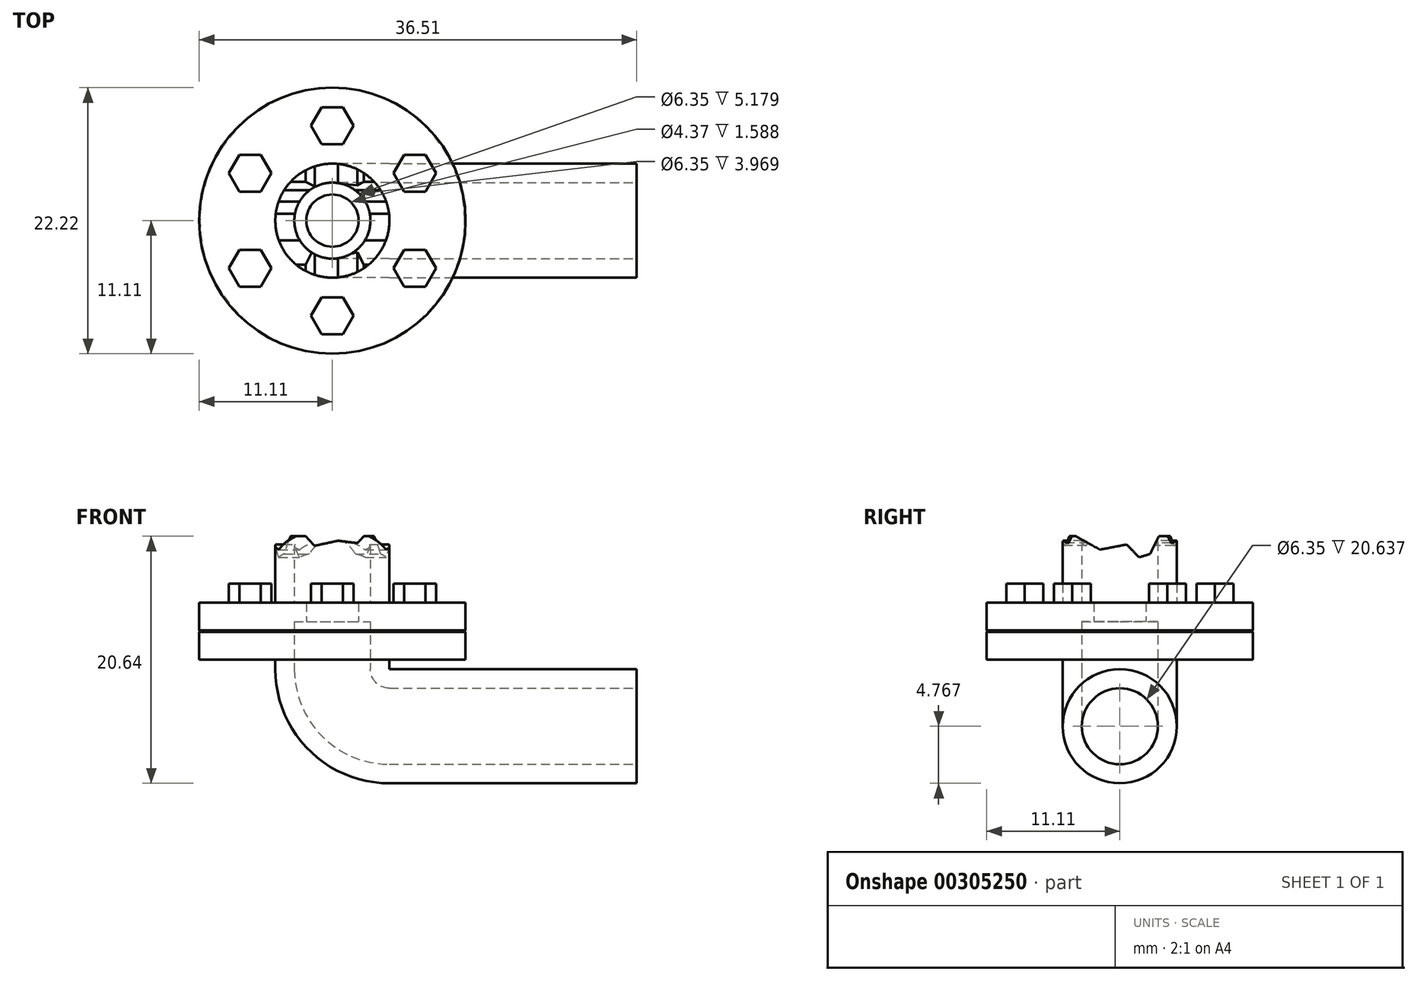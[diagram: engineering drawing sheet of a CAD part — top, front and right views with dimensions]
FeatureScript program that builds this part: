
annotation { "Feature Type Name" : "Feature", "Feature Type Description" : "" }
export const myFeature = defineFeature(function(context is Context, id is Id, definition is map)
    precondition{}
    {
        {
            var Q0;
            Q0=qCreatedBy(makeId("Front.planeOp"),FACE);
            var sketch = newSketch(context, id + "F0", { "sketchPlane" : qUnion([Q0])});
            skLineSegment(sketch, "E0", {"start": v(0, 0) * mm, "end": v(0, 11.11) * mm, "construction": true});
            skLineSegment(sketch, "E1", {"start": v(3.17, 11.11) * mm, "end": v(4.76, 11.11) * mm});
            skLineSegment(sketch, "E2", {"start": v(4.76, 11.11) * mm, "end": v(4.76, 5.56) * mm});
            skLineSegment(sketch, "E3", {"start": v(4.76, 5.56) * mm, "end": v(11.11, 5.56) * mm});
            skLineSegment(sketch, "E4", {"start": v(11.11, 5.56) * mm, "end": v(11.11, 3.24) * mm});
            skLineSegment(sketch, "E5", {"start": v(11.11, 3.24) * mm, "end": v(11.05, 3.18) * mm});
            skLineSegment(sketch, "E6", {"start": v(11.05, 3.18) * mm, "end": v(11.11, 3.11) * mm});
            skLineSegment(sketch, "E7", {"start": v(11.11, 3.11) * mm, "end": v(11.11, 0.8) * mm});
            skLineSegment(sketch, "E8", {"start": v(11.11, 0.8) * mm, "end": v(4.76, 0.8) * mm});
            skLineSegment(sketch, "E9", {"start": v(4.76, 0.8) * mm, "end": v(4.76, 0) * mm});
            skLineSegment(sketch, "E10", {"start": v(4.76, 0) * mm, "end": v(3.18, 0) * mm});
            skLineSegment(sketch, "E11", {"start": v(3.18, 0) * mm, "end": v(3.17, 5.56) * mm});
            skLineSegment(sketch, "E12", {"start": v(3.17, 5.56) * mm, "end": v(2.18, 5.56) * mm});
            skLineSegment(sketch, "E13", {"start": v(2.18, 3.97) * mm, "end": v(2.18, 5.56) * mm});
            skLineSegment(sketch, "E14", {"start": v(2.18, 3.97) * mm, "end": v(3.17, 3.97) * mm});
            skLineSegment(sketch, "E15", {"start": v(3.18, 3.97) * mm, "end": v(3.17, 11.11) * mm});
            skPoint(sketch, "E16", {"position": v(2.18, 4.76) * mm});
            skSolve(sketch);
        }
        {
            var Q0;
            {var subQ0=sQuery(id+"F0.wireOp",EDGE,"E1");Q0=makeQuery(id+"F0.imprint","IMPRINT",FACE,{"disambiguationData":[TD([[makeQuery(id+"F0.imprint","IMPRINT",EDGE,{"derivedFrom":subQ0}),-1.0]])]});}
            var Q1;
            {var subQ0=sQuery(id+"F0.wireOp",EDGE,"E12");Q1=makeQuery(id+"F0.imprint","IMPRINT",FACE,{"disambiguationData":[TD([[makeQuery(id+"F0.imprint","IMPRINT",EDGE,{"derivedFrom":subQ0}),1.0]])]});}
            var Q2;
            Q2=sQuery(id+"F0.wireOp",EDGE,"E0");
            revolve(context, id + "F1", {"entities" : qUnion([Q0, Q1]), "axis" : qUnion([Q2]), "revolveType" : RevolveType.FULL});
        }
        {
            var Q0;
            Q0=makeQuery(id+"F1.opRevolve","SWEPT_FACE",FACE,{"disambiguationData":[OSD([sQuery(id+"F0.wireOp",EDGE,"E3")])]});
            var sketch = newSketch(context, id + "F2", { "sketchPlane" : qUnion([Q0])});
            skCircle(sketch, "E17.cCircle", {"center": v(0, 7.94) * mm, "radius": 1.54 * mm, "construction": true});
            skLineSegment(sketch, "E17.0", {"start": v(-0.89, 9.48) * mm, "end": v(0.89, 9.48) * mm});
            skLineSegment(sketch, "E17.1", {"start": v(0.89, 9.48) * mm, "end": v(1.78, 7.94) * mm});
            skLineSegment(sketch, "E17.2", {"start": v(1.78, 7.94) * mm, "end": v(0.89, 6.4) * mm});
            skLineSegment(sketch, "E17.3", {"start": v(0.89, 6.4) * mm, "end": v(-0.89, 6.4) * mm});
            skLineSegment(sketch, "E17.4", {"start": v(-0.89, 6.4) * mm, "end": v(-1.78, 7.94) * mm});
            skLineSegment(sketch, "E17.5", {"start": v(-1.78, 7.94) * mm, "end": v(-0.89, 9.48) * mm});
            skPoint(sketch, "E17.0.midPoint", {"position": v(0, 9.48) * mm});
            skLineSegment(sketch, "E18", {"start": v(0, 4.76) * mm, "end": v(0, 11.11) * mm, "construction": true});
            skLineSegment(sketch, "E19.1.0", {"start": v(-8.65, 3.97) * mm, "end": v(-7.76, 5.5) * mm});
            skLineSegment(sketch, "E19.1.1", {"start": v(-7.76, 2.43) * mm, "end": v(-8.65, 3.97) * mm});
            skLineSegment(sketch, "E19.1.2", {"start": v(-5.99, 2.43) * mm, "end": v(-7.76, 2.43) * mm});
            skLineSegment(sketch, "E19.1.3", {"start": v(-5.1, 3.97) * mm, "end": v(-5.99, 2.43) * mm});
            skLineSegment(sketch, "E19.1.4", {"start": v(-5.99, 5.5) * mm, "end": v(-5.1, 3.97) * mm});
            skLineSegment(sketch, "E19.1.5", {"start": v(-7.76, 5.5) * mm, "end": v(-5.99, 5.5) * mm});
            skLineSegment(sketch, "E19.2.0", {"start": v(-7.76, -5.5) * mm, "end": v(-8.65, -3.97) * mm});
            skLineSegment(sketch, "E19.2.1", {"start": v(-5.99, -5.5) * mm, "end": v(-7.76, -5.5) * mm});
            skLineSegment(sketch, "E19.2.2", {"start": v(-5.1, -3.97) * mm, "end": v(-5.99, -5.5) * mm});
            skLineSegment(sketch, "E19.2.3", {"start": v(-5.99, -2.43) * mm, "end": v(-5.1, -3.97) * mm});
            skLineSegment(sketch, "E19.2.4", {"start": v(-7.76, -2.43) * mm, "end": v(-5.99, -2.43) * mm});
            skLineSegment(sketch, "E19.2.5", {"start": v(-8.65, -3.97) * mm, "end": v(-7.76, -2.43) * mm});
            skLineSegment(sketch, "E19.3.0", {"start": v(0.89, -9.48) * mm, "end": v(-0.89, -9.48) * mm});
            skLineSegment(sketch, "E19.3.1", {"start": v(1.78, -7.94) * mm, "end": v(0.89, -9.48) * mm});
            skLineSegment(sketch, "E19.3.2", {"start": v(0.89, -6.4) * mm, "end": v(1.78, -7.94) * mm});
            skLineSegment(sketch, "E19.3.3", {"start": v(-0.89, -6.4) * mm, "end": v(0.89, -6.4) * mm});
            skLineSegment(sketch, "E19.3.4", {"start": v(-1.78, -7.94) * mm, "end": v(-0.89, -6.4) * mm});
            skLineSegment(sketch, "E19.3.5", {"start": v(-0.89, -9.48) * mm, "end": v(-1.78, -7.94) * mm});
            skLineSegment(sketch, "E19.4.0", {"start": v(8.65, -3.97) * mm, "end": v(7.76, -5.5) * mm});
            skLineSegment(sketch, "E19.4.1", {"start": v(7.76, -2.43) * mm, "end": v(8.65, -3.97) * mm});
            skLineSegment(sketch, "E19.4.2", {"start": v(5.99, -2.43) * mm, "end": v(7.76, -2.43) * mm});
            skLineSegment(sketch, "E19.4.3", {"start": v(5.1, -3.97) * mm, "end": v(5.99, -2.43) * mm});
            skLineSegment(sketch, "E19.4.4", {"start": v(5.99, -5.5) * mm, "end": v(5.1, -3.97) * mm});
            skLineSegment(sketch, "E19.4.5", {"start": v(7.76, -5.5) * mm, "end": v(5.99, -5.5) * mm});
            skLineSegment(sketch, "E19.5.0", {"start": v(7.76, 5.5) * mm, "end": v(8.65, 3.97) * mm});
            skLineSegment(sketch, "E19.5.1", {"start": v(5.99, 5.5) * mm, "end": v(7.76, 5.5) * mm});
            skLineSegment(sketch, "E19.5.2", {"start": v(5.1, 3.97) * mm, "end": v(5.99, 5.5) * mm});
            skLineSegment(sketch, "E19.5.3", {"start": v(5.99, 2.43) * mm, "end": v(5.1, 3.97) * mm});
            skLineSegment(sketch, "E19.5.4", {"start": v(7.76, 2.43) * mm, "end": v(5.99, 2.43) * mm});
            skLineSegment(sketch, "E19.5.5", {"start": v(8.65, 3.97) * mm, "end": v(7.76, 2.43) * mm});
            skPoint(sketch, "E19.center", {"position": v(0, 0) * mm});
            skSolve(sketch);
        }
        {
            var Q0;
            Q0 = qSketchRegion(id + "F2", true);
            extrude(context, id + "F3", {"entities" : qUnion([Q0]), "operationType" : NewBodyOperationType.ADD, "depth" : 1.59 * mm});
        }
        {
            var Q0;
            Q0=qCreatedBy(makeId("Right.planeOp"),FACE);
            var sketch = newSketch(context, id + "F4", { "sketchPlane" : qUnion([Q0])});
            skLineSegment(sketch, "E20", {"start": v(-4.76, 5.56) * mm, "end": v(-4.76, 11.11) * mm});
            skLineSegment(sketch, "E21", {"start": v(4.76, 11.11) * mm, "end": v(4.76, 5.56) * mm});
            skLineSegment(sketch, "E22", {"start": v(3.25, 11.11) * mm, "end": v(2.53, 9.63) * mm});
            skLineSegment(sketch, "E23", {"start": v(2.53, 9.63) * mm, "end": v(1.6, 9.35) * mm});
            skLineSegment(sketch, "E24", {"start": v(1.6, 9.35) * mm, "end": v(0.58, 10.42) * mm});
            skLineSegment(sketch, "E25", {"start": v(0.58, 10.42) * mm, "end": v(-1.65, 9.99) * mm});
            skLineSegment(sketch, "E26", {"start": v(-1.65, 9.99) * mm, "end": v(-3.69, 11.11) * mm});
            skLineSegment(sketch, "E27", {"start": v(-3.69, 11.11) * mm, "end": v(3.25, 11.11) * mm});
            skLineSegment(sketch, "E28.0.0", {"start": v(-4.76, 11.11) * mm, "end": v(4.76, 11.11) * mm});
            skSolve(sketch);
        }
        {
            var Q0;
            Q0 = qSketchRegion(id + "F4", true);
            extrude(context, id + "F5", {"entities" : qUnion([Q0]), "operationType" : NewBodyOperationType.REMOVE, "oppositeDirection" : true, "depth" : 25.4 * mm, "symmetric" : true});
        }
        {
            var Q0;
            Q0=qCreatedBy(makeId("Front.planeOp"),FACE);
            var sketch = newSketch(context, id + "F6", { "sketchPlane" : qUnion([Q0])});
            skLineSegment(sketch, "E29", {"start": v(-4.76, 5.56) * mm, "end": v(-4.76, 10.3) * mm});
            skLineSegment(sketch, "E30", {"start": v(4.76, 10.3) * mm, "end": v(4.76, 5.56) * mm});
            skLineSegment(sketch, "E31.0.0", {"start": v(3.01, 11.11) * mm, "end": v(-3.01, 11.11) * mm});
            skLineSegment(sketch, "E31.0.1", {"start": v(-3.01, 11.11) * mm, "end": v(3.01, 11.11) * mm});
            skLineSegment(sketch, "E32", {"start": v(-2.24, 11.11) * mm, "end": v(-1.48, 10.31) * mm});
            skLineSegment(sketch, "E33", {"start": v(-1.48, 10.31) * mm, "end": v(0.48, 10.73) * mm});
            skLineSegment(sketch, "E34", {"start": v(0.48, 10.73) * mm, "end": v(2.09, 10.53) * mm});
            skLineSegment(sketch, "E35", {"start": v(2.09, 10.53) * mm, "end": v(2.62, 11.11) * mm});
            skSolve(sketch);
        }
        {
            var Q0;
            Q0 = qSketchRegion(id + "F6", true);
            extrude(context, id + "F7", {"entities" : qUnion([Q0]), "operationType" : NewBodyOperationType.REMOVE, "oppositeDirection" : true, "depth" : 25.4 * mm, "symmetric" : true});
        }
        {
            var Q0;
            Q0=qCreatedBy(makeId("Front.planeOp"),FACE);
            var sketch = newSketch(context, id + "F8", { "sketchPlane" : qUnion([Q0])});
            skLineSegment(sketch, "E36", {"start": v(0, 0) * mm, "end": v(0, 0) * mm});
            skLineSegment(sketch, "E37", {"start": v(4.76, -4.76) * mm, "end": v(25.4, -4.76) * mm});
            skPoint(sketch, "E38.visualSharp", {"position": v(0, -4.76) * mm});
            skArc(sketch, "E38.filletArc", {"start": v(0, 0) * mm, "mid": v(1.4, -3.37) * mm, "end": v(4.76, -4.76) * mm});
            skSolve(sketch);
        }
        {
            var Q0;
            Q0=makeQuery(id+"F1.opRevolve","SWEPT_FACE",FACE,{"disambiguationData":[OSD([sQuery(id+"F0.wireOp",EDGE,"E10")])]});
            var Q1;
            Q1=sQuery(id+"F8.wireOp",EDGE,"E36");
            var Q2;
            Q2=sQuery(id+"F8.wireOp",EDGE,"E38.filletArc");
            var Q3;
            Q3=sQuery(id+"F8.wireOp",EDGE,"E37");
            sweep(context, id + "F9", {"operationType" : NewBodyOperationType.ADD, "profiles" : qUnion([Q0]), "path" : qUnion([Q1, Q2, Q3])});
        }
    });
